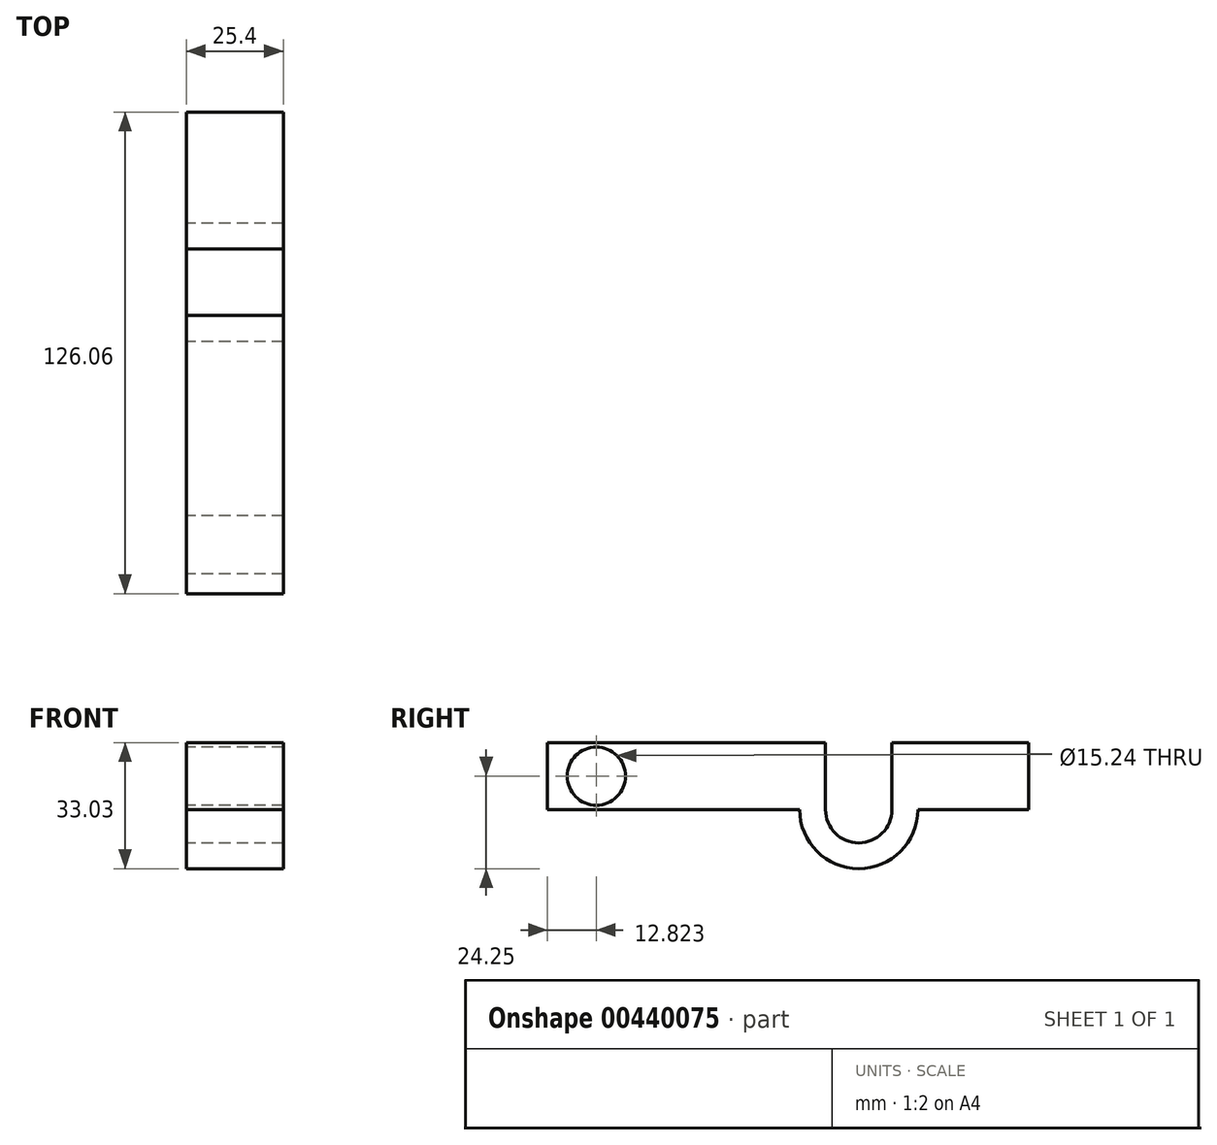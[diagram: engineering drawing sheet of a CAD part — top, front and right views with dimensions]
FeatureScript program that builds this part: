
annotation { "Feature Type Name" : "Feature", "Feature Type Description" : "" }
export const myFeature = defineFeature(function(context is Context, id is Id, definition is map)
    precondition{}
    {
        {
            var Q0;
            Q0=qCreatedBy(makeId("Right.planeOp"),FACE);
            var sketch = newSketch(context, id + "F0", { "sketchPlane" : qUnion([Q0])});
            skLineSegment(sketch, "E0", {"start": v(-66.05, 21.3) * mm, "end": v(0, 21.3) * mm});
            skLineSegment(sketch, "E1", {"start": v(-66.05, 21.3) * mm, "end": v(-66.05, 3.74) * mm});
            skLineSegment(sketch, "E2", {"start": v(-66.05, 3.74) * mm, "end": v(0, 3.74) * mm});
            skLineSegment(sketch, "E3", {"start": v(0, 3.74) * mm, "end": v(30.94, 3.74) * mm});
            skArc(sketch, "E4", {"start": v(0, 3.74) * mm, "mid": v(15.47, -11.73) * mm, "end": v(30.94, 3.74) * mm});
            skLineSegment(sketch, "E5", {"start": v(0, 21.3) * mm, "end": v(6.76, 21.3) * mm});
            skLineSegment(sketch, "E6", {"start": v(6.76, 21.3) * mm, "end": v(6.76, 8.63) * mm});
            skLineSegment(sketch, "E7", {"start": v(6.76, 8.63) * mm, "end": v(6.76, 3.74) * mm});
            skCircle(sketch, "E8", {"center": v(15.47, 3.74) * mm, "radius": 8.7 * mm});
            skLineSegment(sketch, "E9", {"start": v(24.18, 3.74) * mm, "end": v(24.18, 21.3) * mm});
            skLineSegment(sketch, "E10", {"start": v(24.18, 21.3) * mm, "end": v(60, 21.3) * mm});
            skLineSegment(sketch, "E11", {"start": v(60, 21.3) * mm, "end": v(60, 3.74) * mm});
            skLineSegment(sketch, "E12", {"start": v(60, 3.74) * mm, "end": v(30.94, 3.74) * mm});
            skSolve(sketch);
        }
        {
            var Q0;
            Q0=makeQuery(id+"F0.imprint","IMPRINT",FACE,{"disambiguationData":[TD([[makeQuery(id+"F0.imprint","IMPRINT",EDGE,{"derivedFrom":sQuery(id+"F0.wireOp",EDGE,"E0")}),-1.0]])]});
            var Q1;
            {var subQ0=sQuery(id+"F0.wireOp",EDGE,"E9");Q1=makeQuery(id+"F0.imprint","IMPRINT",FACE,{"disambiguationData":[TD([[makeQuery(id+"F0.imprint","IMPRINT",EDGE,{"derivedFrom":subQ0}),-1.0]])]});}
            var Q2;
            {var subQ0=sQuery(id+"F0.wireOp",EDGE,"E4");Q2=makeQuery(id+"F0.imprint","IMPRINT",FACE,{"disambiguationData":[TD([[makeQuery(id+"F0.imprint","IMPRINT",EDGE,{"derivedFrom":subQ0}),1.0]])]});}
            extrude(context, id + "F1", {"entities" : qUnion([Q0, Q1, Q2]), "depth" : 25.4 * mm});
        }
        {
            var Q0;
            Q0=makeQuery(id+"F1.opExtrude","CAP_FACE",FACE,{"disambiguationData":[OSD([sQuery(id+"F0.wireOp",EDGE,"E0"),sQuery(id+"F0.wireOp",EDGE,"E1"),sQuery(id+"F0.wireOp",EDGE,"E2"),sQuery(id+"F0.wireOp",EDGE,"E4"),sQuery(id+"F0.wireOp",EDGE,"E5"),sQuery(id+"F0.wireOp",EDGE,"E6"),sQuery(id+"F0.wireOp",EDGE,"E7"),sQuery(id+"F0.wireOp",EDGE,"E8"),sQuery(id+"F0.wireOp",EDGE,"E9"),sQuery(id+"F0.wireOp",EDGE,"E10"),sQuery(id+"F0.wireOp",EDGE,"E11"),sQuery(id+"F0.wireOp",EDGE,"E12")])],"isStart":true});
            var sketch = newSketch(context, id + "F2", { "sketchPlane" : qUnion([Q0])});
            skPoint(sketch, "E13.centerSnap0", {"position": v(-60, 12.52) * mm});
            skCircle(sketch, "E14", {"center": v(53.23, 12.52) * mm, "radius": 7.62 * mm});
            skPoint(sketch, "E14.centerSnap0", {"position": v(66.05, 12.52) * mm});
            skPoint(sketch, "E14.perimeterSnap0", {"position": v(66.05, 12.52) * mm});
            skPoint(sketch, "E13.center.orphan", {"position": v(-49.07, 12.52) * mm});
            skSolve(sketch);
        }
        {
            var Q0;
            Q0 = qSketchRegion(id + "F2", true);
            extrude(context, id + "F3", {"entities" : qUnion([Q0]), "operationType" : NewBodyOperationType.REMOVE, "endBound" : BoundingType.THROUGH_ALL, "oppositeDirection" : true, "depth" : 25.4 * mm});
        }
    });
